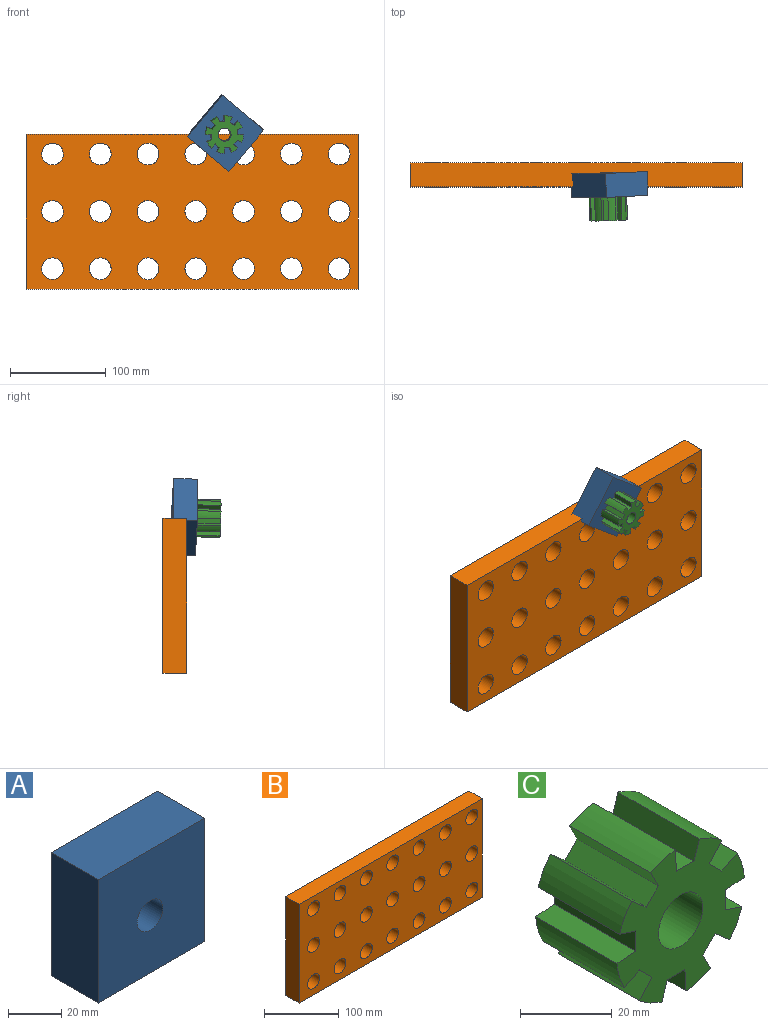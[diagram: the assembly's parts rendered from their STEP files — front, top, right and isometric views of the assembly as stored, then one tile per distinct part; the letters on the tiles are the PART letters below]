
ASSEMBLY  parts=3 mates=1
PART A: 7 faces, bbox 56.7x25x56.7 mm
  f0: plane 56.69x25mm, normal (1,0,0), area 1417.2mm2, adj f1,f3,f4,f5
  f1: plane 56.69x25mm, normal (0,0,1), area 1417.2mm2, adj f0,f2,f4,f5
  f2: plane 56.69x25mm, normal (-1,0,0), area 1417.2mm2, adj f1,f3,f4,f5
  f3: plane 56.69x25mm, normal (0,0,-1), area 1417.2mm2, adj f0,f2,f4,f5
  f4: plane 56.69x56.69mm, normal (0,-1,0), area 3067.7mm2, adj f0,f1,f2,f3,f6
  f5: plane 56.69x56.69mm, normal (0,1,0), area 3067.7mm2, adj f0,f1,f2,f3,f6
  f6: cylinder r=6.81mm len=25mm, axis (0,-1,0), area 1070.1mm2, adj f4,f5
PART B: 27 faces, bbox 347.4x25x162.2 mm
  f0: cylinder r=11.36mm len=25mm, axis (0,-1,0), area 1784.8mm2, adj f24,f25
  f1: cylinder r=11.36mm len=25mm, axis (0,-1,0), area 1784.8mm2, adj f24,f25
  f2: cylinder r=11.36mm len=25mm, axis (0,-1,0), area 1784.8mm2, adj f24,f25
  f3: cylinder r=11.36mm len=25mm, axis (0,-1,0), area 1784.8mm2, adj f24,f25
  f4: cylinder r=11.36mm len=25mm, axis (0,-1,0), area 1784.8mm2, adj f24,f25
  f5: cylinder r=11.36mm len=25mm, axis (0,-1,0), area 1784.8mm2, adj f24,f25
  f6: cylinder r=11.36mm len=25mm, axis (0,-1,0), area 1784.8mm2, adj f24,f25
  f7: cylinder r=11.36mm len=25mm, axis (0,-1,0), area 1784.8mm2, adj f24,f25
  f8: cylinder r=11.36mm len=25mm, axis (0,-1,0), area 1784.8mm2, adj f24,f25
  f9: cylinder r=11.36mm len=25mm, axis (0,-1,0), area 1784.8mm2, adj f24,f25
  f10: cylinder r=11.36mm len=25mm, axis (0,-1,0), area 1784.8mm2, adj f24,f25
  f11: cylinder r=11.36mm len=25mm, axis (0,-1,0), area 1784.8mm2, adj f24,f25
  f12: cylinder r=11.36mm len=25mm, axis (0,-1,0), area 1784.8mm2, adj f24,f25
  f13: cylinder r=11.36mm len=25mm, axis (0,-1,0), area 1784.8mm2, adj f24,f25
  f14: cylinder r=11.36mm len=25mm, axis (0,-1,0), area 1784.8mm2, adj f24,f25
  f15: cylinder r=11.36mm len=25mm, axis (0,-1,0), area 1784.8mm2, adj f24,f25
  f16: cylinder r=11.36mm len=25mm, axis (0,-1,0), area 1784.8mm2, adj f24,f25
  f17: cylinder r=11.36mm len=25mm, axis (0,-1,0), area 1784.8mm2, adj f24,f25
  f18: cylinder r=11.36mm len=25mm, axis (0,-1,0), area 1784.8mm2, adj f24,f25
  f19: cylinder r=11.36mm len=25mm, axis (0,-1,0), area 1784.8mm2, adj f24,f25
  f20: plane 162.17x25mm, normal (1,0,0), area 4054.3mm2, adj f21,f23,f24,f25
  f21: plane 347.38x25mm, normal (0,0,1), area 8684.5mm2, adj f20,f22,f24,f25
  f22: plane 162.17x25mm, normal (-1,0,0), area 4054.3mm2, adj f21,f23,f24,f25
  f23: plane 347.38x25mm, normal (0,0,-1), area 8684.5mm2, adj f20,f22,f24,f25
  f24: plane 347.38x162.17mm, normal (0,-1,0), area 47817mm2, adj f0,f1,f2,f3,f4,f5,f6,f7
  f25: plane 347.38x162.17mm, normal (0,1,0), area 47817mm2, adj f0,f1,f2,f3,f4,f5,f6,f7
  f26: cylinder r=11.36mm len=25mm, axis (0,-1,0), area 1784.8mm2, adj f24,f25
PART C: 35 faces, bbox 39.2x25x39.2 mm
  f0: cylinder r=19.67mm len=25mm, axis (0,1,0), area 199.5mm2, adj f2,f3,f12,f32
  f1: cylinder r=19.67mm len=25mm, axis (0,1,0), area 199.5mm2, adj f2,f3,f29,f33
  f2: plane 39.19x39.19mm, normal (0,-1,0), area 776.3mm2, adj f0,f1,f4,f5,f6,f7,f8,f9
  f3: plane 39.19x39.19mm, normal (0,1,0), area 776.3mm2, adj f0,f1,f4,f5,f6,f7,f8,f9
  f4: cylinder r=19.67mm len=25mm, axis (0,1,0), area 199.5mm2, adj f2,f3,f26,f30
  f5: cylinder r=19.67mm len=25mm, axis (0,1,0), area 199.5mm2, adj f2,f3,f23,f27
  f6: cylinder r=19.67mm len=25mm, axis (0,1,0), area 199.5mm2, adj f2,f3,f20,f24
  f7: cylinder r=19.67mm len=25mm, axis (0,1,0), area 199.5mm2, adj f2,f3,f17,f21
  f8: cylinder r=19.67mm len=25mm, axis (0,1,0), area 199.5mm2, adj f2,f3,f14,f18
  f9: cylinder r=19.67mm len=25mm, axis (0,1,0), area 199.5mm2, adj f2,f3,f11,f15
  f10: cylinder r=6.81mm len=25mm, axis (0,-1,0), area 1070.1mm2, adj f2,f3
  f11: plane 25x5.04mm, normal (0.31,0,0.95), area 132.5mm2, adj f2,f3,f9,f13
  f12: plane 25x5.82mm, normal (0.06,0,-1), area 145.8mm2, adj f0,f2,f3,f13
  f13: plane 25x5.37mm, normal (1,0,0), area 134.2mm2, adj f2,f3,f11,f12
  f14: plane 25x4.72mm, normal (0.89,0,0.45), area 132.5mm2, adj f2,f3,f8,f16
  f15: plane 25x4.38mm, normal (-0.66,0,-0.75), area 145.8mm2, adj f2,f3,f9,f16
  f16: plane 25x3.8mm, normal (0.71,0,-0.71), area 134.2mm2, adj f2,f3,f14,f15
  f17: plane 25x5.04mm, normal (0.95,0,-0.31), area 132.5mm2, adj f2,f3,f7,f19
  f18: plane 25x5.82mm, normal (-1,0,-0.06), area 145.8mm2, adj f2,f3,f8,f19
  f19: plane 25x5.37mm, normal (0,0,-1), area 134.2mm2, adj f2,f3,f17,f18
  f20: plane 25x4.72mm, normal (0.45,0,-0.89), area 132.5mm2, adj f2,f3,f6,f22
  f21: plane 25x4.38mm, normal (-0.75,0,0.66), area 145.8mm2, adj f2,f3,f7,f22
  f22: plane 25x3.8mm, normal (-0.71,0,-0.71), area 134.2mm2, adj f2,f3,f20,f21
  f23: plane 25x5.04mm, normal (-0.31,0,-0.95), area 132.5mm2, adj f2,f3,f5,f25
  f24: plane 25x5.82mm, normal (-0.06,0,1), area 145.8mm2, adj f2,f3,f6,f25
  f25: plane 25x5.37mm, normal (-1,0,0), area 134.2mm2, adj f2,f3,f23,f24
  f26: plane 25x4.72mm, normal (-0.89,0,-0.45), area 132.5mm2, adj f2,f3,f4,f28
  f27: plane 25x4.38mm, normal (0.66,0,0.75), area 145.8mm2, adj f2,f3,f5,f28
  f28: plane 25x3.8mm, normal (-0.71,0,0.71), area 134.2mm2, adj f2,f3,f26,f27
  f29: plane 25x5.04mm, normal (-0.95,0,0.31), area 132.5mm2, adj f1,f2,f3,f31
  f30: plane 25x5.82mm, normal (1,0,0.06), area 145.8mm2, adj f2,f3,f4,f31
  f31: plane 25x5.37mm, normal (0,0,1), area 134.2mm2, adj f2,f3,f29,f30
  f32: plane 25x4.72mm, normal (-0.45,0,0.89), area 132.5mm2, adj f0,f2,f3,f34
  f33: plane 25x4.38mm, normal (0.75,0,-0.66), area 145.8mm2, adj f1,f2,f3,f34
  f34: plane 25x3.8mm, normal (0.71,0,0.71), area 134.2mm2, adj f2,f3,f32,f33
PLACE A rot(axis=(0.02,1,0.05),40.1deg) t=(50.71,-8.47,6.34)mm
PLACE B at identity
PLACE C rot(axis=(-0.91,-0.01,-0.42),178deg) t=(45.34,-85.81,91.66)mm
MATE pin_slot A.f6 <-> C.f0  axis (0.03,-1,-0.02) through (33.42,-35.04,48.06)mm
